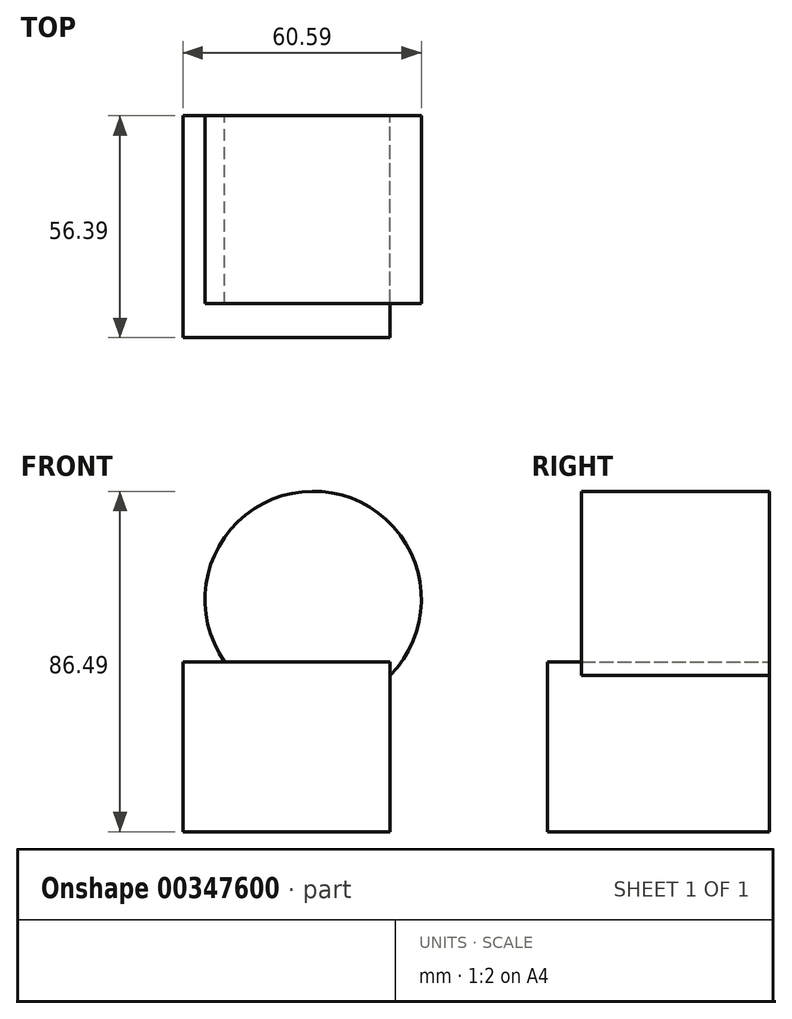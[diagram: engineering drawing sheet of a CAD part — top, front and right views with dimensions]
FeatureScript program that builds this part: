
annotation { "Feature Type Name" : "Feature", "Feature Type Description" : "" }
export const myFeature = defineFeature(function(context is Context, id is Id, definition is map)
    precondition{}
    {
        {
            var Q0;
            Q0=qCreatedBy(makeId("Front.planeOp"),FACE);
            var sketch = newSketch(context, id + "F0", { "sketchPlane" : qUnion([Q0])});
            skLineSegment(sketch, "E0.bottom", {"start": v(-26.48, 15.83) * mm, "end": v(26.2, 15.83) * mm});
            skLineSegment(sketch, "E0.top", {"start": v(-26.48, -27.34) * mm, "end": v(26.2, -27.34) * mm});
            skLineSegment(sketch, "E0.left", {"start": v(-26.48, 15.83) * mm, "end": v(-26.48, -27.34) * mm});
            skLineSegment(sketch, "E0.right", {"start": v(26.2, 15.83) * mm, "end": v(26.2, -27.34) * mm});
            skSolve(sketch);
        }
        {
            var Q0;
            Q0=makeQuery(id+"F0.imprint","IMPRINT",FACE,{"disambiguationData":[TD([[makeQuery(id+"F0.imprint","IMPRINT",EDGE,{"derivedFrom":sQuery(id+"F0.wireOp",EDGE,"E0.bottom")}),-1.0]])]});
            extrude(context, id + "F1", {"entities" : qUnion([Q0]), "depth" : 56.4 * mm});
        }
        {
            var Q0;
            Q0=qCreatedBy(makeId("Front.planeOp"),FACE);
            var sketch = newSketch(context, id + "F2", { "sketchPlane" : qUnion([Q0])});
            skCircle(sketch, "E1", {"center": v(6.62, 31.66) * mm, "radius": 27.5 * mm});
            skSolve(sketch);
        }
        {
            var Q0;
            Q0=makeQuery(id+"F2.imprint","IMPRINT",FACE,{"disambiguationData":[TD([[makeQuery(id+"F2.imprint","IMPRINT",EDGE,{"derivedFrom":sQuery(id+"F2.wireOp",EDGE,"E1")}),1.0]])]});
            extrude(context, id + "F3", {"entities" : qUnion([Q0]), "operationType" : NewBodyOperationType.ADD, "depth" : 47.75 * mm});
        }
    });
